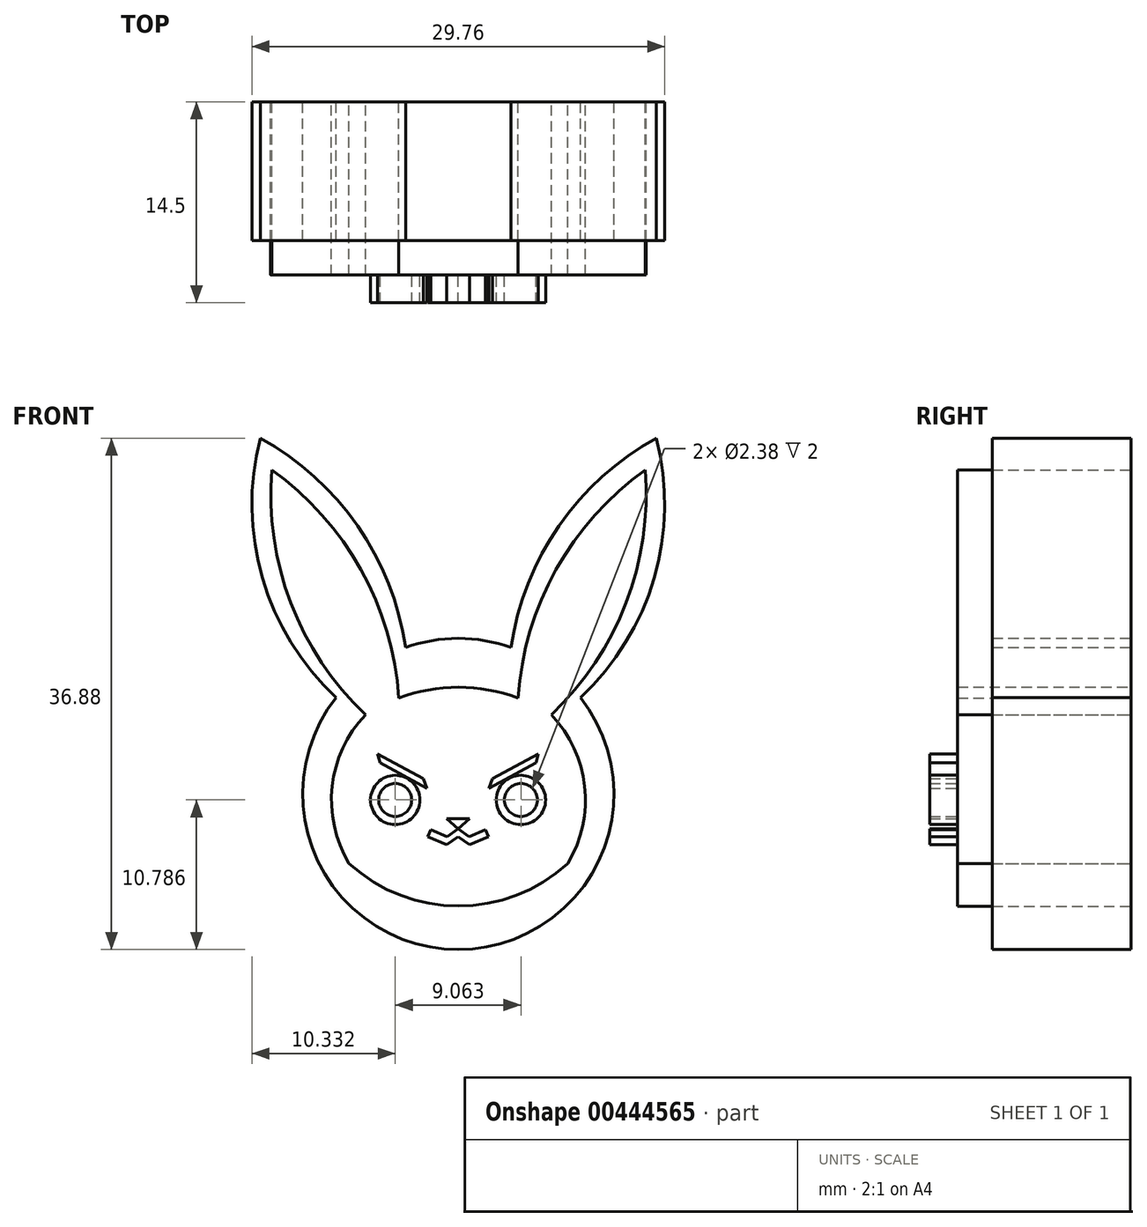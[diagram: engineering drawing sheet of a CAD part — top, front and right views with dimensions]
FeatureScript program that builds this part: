
annotation { "Feature Type Name" : "Feature", "Feature Type Description" : "" }
export const myFeature = defineFeature(function(context is Context, id is Id, definition is map)
    precondition{}
    {
        {
            var Q0;
            Q0=qCreatedBy(makeId("Front.planeOp"),FACE);
            var sketch = newSketch(context, id + "F0", { "sketchPlane" : qUnion([Q0])});
            skPoint(sketch, "E0.middle", {"position": v(0, 0) * mm});
            skPoint(sketch, "E1.visualSharp", {"position": v(-25, 25) * mm});
            skPoint(sketch, "E2.visualSharp", {"position": v(25, 25) * mm});
            skPoint(sketch, "E3.visualSharp", {"position": v(25, -25) * mm});
            skPoint(sketch, "E4.visualSharp", {"position": v(-25, -25) * mm});
            skArc(sketch, "E5", {"start": v(-8.8, 1.17) * mm, "mid": v(0, -17.01) * mm, "end": v(8.8, 1.17) * mm});
            skArc(sketch, "E6", {"start": v(-14.27, 19.87) * mm, "mid": v(-14.12, 9.76) * mm, "end": v(-8.8, 1.17) * mm});
            skArc(sketch, "E7.MirrorCS", {"start": v(-14.27, 19.87) * mm, "mid": v(-7.26, 13.55) * mm, "end": v(-3.8, 4.77) * mm});
            skArc(sketch, "E8.MirrorCS", {"start": v(14.27, 19.87) * mm, "mid": v(14.12, 9.76) * mm, "end": v(8.8, 1.17) * mm});
            skArc(sketch, "E9.MirrorCS", {"start": v(14.27, 19.87) * mm, "mid": v(7.26, 13.55) * mm, "end": v(3.8, 4.77) * mm});
            skArc(sketch, "E10.trimOffspring", {"start": v(3.8, 4.77) * mm, "mid": v(0, 5.43) * mm, "end": v(-3.8, 4.77) * mm});
            skSolve(sketch);
        }
        {
            var Q0;
            Q0=qCreatedBy(makeId("Front.planeOp"),FACE);
            var sketch = newSketch(context, id + "F1", { "sketchPlane" : qUnion([Q0])});
            skArc(sketch, "E11", {"start": v(-6.7, -0.08) * mm, "mid": v(-9.1, -5.24) * mm, "end": v(-7.87, -10.8) * mm});
            skArc(sketch, "E12", {"start": v(4.31, 1.13) * mm, "mid": v(0.01, 1.9) * mm, "end": v(-4.29, 1.13) * mm});
            skArc(sketch, "E13.MirrorCS", {"start": v(6.71, -0.08) * mm, "mid": v(9.11, -5.24) * mm, "end": v(7.9, -10.8) * mm});
            skArc(sketch, "E14", {"start": v(-7.87, -10.8) * mm, "mid": v(0.01, -13.88) * mm, "end": v(7.9, -10.8) * mm});
            skArc(sketch, "E15", {"start": v(-13.44, 17.71) * mm, "mid": v(-12.1, 8.05) * mm, "end": v(-6.7, -0.08) * mm});
            skArc(sketch, "E16.MirrorCS", {"start": v(-13.58, 17.65) * mm, "mid": v(-7.06, 10.44) * mm, "end": v(-4.29, 1.13) * mm});
            skArc(sketch, "E17.MirrorCS", {"start": v(13.6, 17.65) * mm, "mid": v(7.08, 10.44) * mm, "end": v(4.31, 1.13) * mm});
            skArc(sketch, "E18.MirrorCS", {"start": v(13.47, 17.71) * mm, "mid": v(12.12, 8.05) * mm, "end": v(6.71, -0.08) * mm});
            skSolve(sketch);
        }
        {
            var Q0;
            Q0 = qSketchRegion(id + "F0", true);
            extrude(context, id + "F2", {"entities" : qUnion([Q0]), "depth" : 10 * mm});
        }
        {
            var Q0;
            Q0 = qSketchRegion(id + "F1", true);
            extrude(context, id + "F3", {"entities" : qUnion([Q0]), "depth" : 12.5 * mm});
        }
        {
            var Q0;
            Q0=makeQuery(id+"F3.opExtrude","CAP_FACE",FACE,{"disambiguationData":[OSD([sQuery(id+"F1.wireOp",EDGE,"E11"),sQuery(id+"F1.wireOp",EDGE,"E12"),sQuery(id+"F1.wireOp",EDGE,"E13.MirrorCS"),sQuery(id+"F1.wireOp",EDGE,"E14"),sQuery(id+"F1.wireOp",EDGE,"E15"),sQuery(id+"F1.wireOp",EDGE,"E16.MirrorCS"),sQuery(id+"F1.wireOp",EDGE,"E17.MirrorCS"),sQuery(id+"F1.wireOp",EDGE,"E18.MirrorCS")])],"isStart":false});
            cPlane(context, id + "F4", {"entities" : qUnion([Q0]), "cplaneType" : CPlaneType.OFFSET, "offset" : 0 * mm, "width" : 150 * mm, "height" : 150 * mm});
        }
        {
            var Q0;
            Q0=qCreatedBy(id+"F4.planeOp",FACE);
            var sketch = newSketch(context, id + "F5", { "sketchPlane" : qUnion([Q0])});
            skLineSegment(sketch, "E19", {"start": v(-5.8, -2.92) * mm, "end": v(-2.5, -4.69) * mm});
            skLineSegment(sketch, "E20", {"start": v(-2.5, -4.69) * mm, "end": v(-2.25, -5.4) * mm});
            skLineSegment(sketch, "E21", {"start": v(-2.25, -5.4) * mm, "end": v(-5.63, -3.55) * mm});
            skLineSegment(sketch, "E22", {"start": v(-5.63, -3.55) * mm, "end": v(-5.8, -2.92) * mm});
            skCircle(sketch, "E23", {"center": v(-4.55, -6.22) * mm, "radius": 1.78 * mm});
            skCircle(sketch, "E24", {"center": v(-4.55, -6.22) * mm, "radius": 1.19 * mm});
            skLineSegment(sketch, "E25", {"start": v(-0.02, -7.58) * mm, "end": v(-0.84, -7.58) * mm});
            skLineSegment(sketch, "E26", {"start": v(-0.84, -7.58) * mm, "end": v(-0.02, -8.3) * mm});
            skLineSegment(sketch, "E27", {"start": v(-0.02, -8.3) * mm, "end": v(-0.82, -8.87) * mm});
            skLineSegment(sketch, "E28", {"start": v(-0.82, -8.87) * mm, "end": v(-1.98, -8.37) * mm});
            skLineSegment(sketch, "E29", {"start": v(-1.98, -8.37) * mm, "end": v(-2.2, -8.87) * mm});
            skLineSegment(sketch, "E30", {"start": v(-2.2, -8.87) * mm, "end": v(-0.85, -9.46) * mm});
            skLineSegment(sketch, "E31", {"start": v(-0.85, -9.46) * mm, "end": v(-0.02, -8.87) * mm});
            skLineSegment(sketch, "E32.MirrorCS", {"start": v(-0.02, -7.58) * mm, "end": v(0.81, -7.58) * mm});
            skLineSegment(sketch, "E33.MirrorCS", {"start": v(0.81, -7.58) * mm, "end": v(-0.02, -8.3) * mm});
            skLineSegment(sketch, "E34.MirrorCS", {"start": v(-0.02, -8.3) * mm, "end": v(0.79, -8.87) * mm});
            skLineSegment(sketch, "E35.MirrorCS", {"start": v(0.79, -8.87) * mm, "end": v(1.94, -8.37) * mm});
            skLineSegment(sketch, "E36.MirrorCS", {"start": v(2.16, -8.87) * mm, "end": v(0.82, -9.46) * mm});
            skLineSegment(sketch, "E37.MirrorCS", {"start": v(1.94, -8.37) * mm, "end": v(2.16, -8.87) * mm});
            skLineSegment(sketch, "E38.MirrorCS", {"start": v(0.82, -9.46) * mm, "end": v(-0.02, -8.87) * mm});
            skCircle(sketch, "E39.MirrorC", {"center": v(4.52, -6.22) * mm, "radius": 1.19 * mm});
            skCircle(sketch, "E40.MirrorC", {"center": v(4.52, -6.22) * mm, "radius": 1.78 * mm});
            skLineSegment(sketch, "E41.MirrorCS", {"start": v(2.22, -5.4) * mm, "end": v(5.6, -3.55) * mm});
            skLineSegment(sketch, "E42.MirrorCS", {"start": v(2.47, -4.69) * mm, "end": v(2.22, -5.4) * mm});
            skLineSegment(sketch, "E43.MirrorCS", {"start": v(5.78, -2.92) * mm, "end": v(2.47, -4.69) * mm});
            skLineSegment(sketch, "E44.MirrorCS", {"start": v(5.6, -3.55) * mm, "end": v(5.78, -2.92) * mm});
            skSolve(sketch);
        }
        {
            var Q0;
            Q0 = qSketchRegion(id + "F5", true);
            extrude(context, id + "F6", {"entities" : qUnion([Q0]), "depth" : 2 * mm});
        }
        {
            var Q0;
            Q0=makeQuery(id+"F2.opExtrude","CAP_FACE",FACE,{"disambiguationData":[OSD([sQuery(id+"F0.wireOp",EDGE,"E5"),sQuery(id+"F0.wireOp",EDGE,"E6"),sQuery(id+"F0.wireOp",EDGE,"E7.MirrorCS"),sQuery(id+"F0.wireOp",EDGE,"E8.MirrorCS"),sQuery(id+"F0.wireOp",EDGE,"E9.MirrorCS"),sQuery(id+"F0.wireOp",EDGE,"E10.trimOffspring")])],"isStart":false});
            cPlane(context, id + "F7", {"entities" : qUnion([Q0]), "cplaneType" : CPlaneType.OFFSET, "offset" : 0 * mm, "width" : 150 * mm, "height" : 150 * mm});
        }
    });
